# Revit family: 1703-Codo 90º AIS XPRT
name_source: partatom
category: Uniones de tubería
revit_build: Autodesk Revit 2018 (Build: 20170223_1515(x64)
units: mm (PartAtom-declared; Revit-internal decimal feet)

## family parameters
Compartido = No
Corte con vacíos al cargar = No
Cota de conector redondo = Diámetro de uso
Número OmniClass = 23.60.30.11.14
Se basa en plano de trabajo = No
Siempre vertical = Sí
Tipo de pieza = Codo
Título OmniClass = Pipework Fittings

## types (2) — shared parameters
Accesories Material = LATON
Angle = 90.00°
Code Lookup = 1703
Code Lookup EAN = 1703_EAN
Code Lookup SIZE = 1703_SIZE
Fabricante = Multitubo
IfcClassification = Pipe Fitting
MAsterformat 2014 Description = Ball Valves
Mark Size = 11 mm
Masterformat 2014 Code = 40 05 63
Material Main = LATON
Modelo = MC-1703
NBS Reference Code = 62-64
Nombre de tabla de consulta = M_Pipe Fitting - Generic
OmniClass Description = Pipe Fittings
OnmiClass Code = 23-27 43 00
Radio exterior de unión = 7 mm
UNSPSC Code = 401417
Uniclass 1.4 Code = L71163
Uniclass 1.4 Description = Pipe couplings/connectors
Uniclass 2.0 Code = PR-62-64
Uniclass 2.0 Description = Pipe Fittings
Uniclass 2015 Code = Ac_10_40_63
Uniclass 2015 Name = Pipe fitting
Uniformat II Code = C1030
Uniformat II Description = Fittings
zero-valued in all types: Edition number

## per-type parameters (varying)
| type | Lower Thickness | Upper Thickness |
| Todos DN + DN 20 x 2.00 mm | No | Sí |
| Todos DN + DN 20 x 2.25 mm | Sí | No |
